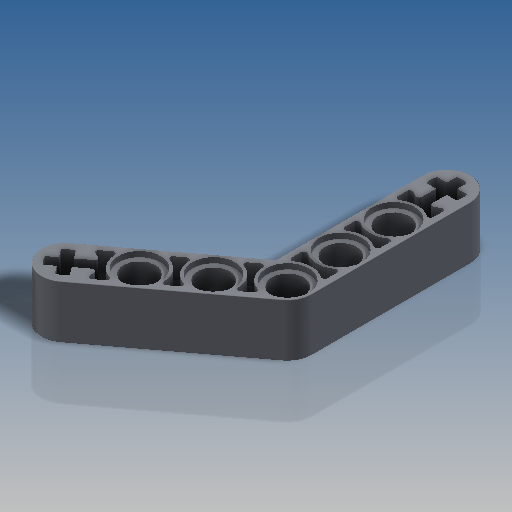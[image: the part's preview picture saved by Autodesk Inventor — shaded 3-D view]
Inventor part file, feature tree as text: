
AUTODESK INVENTOR PART (.ipt)
format: ipt  version: 2019.4 (Build 234330000, 330)  size: 444,928 bytes
history: native  units: mm
features: extrude x3, sketch x2, mirror x1, pattern_circular x1, fillet x1, projected_geometry x1
ambient origin geometry x8: Origin, YZ Plane, XZ Plane, XY Plane, X Axis, Y Axis, Z Axis, Center Point
bodies: Solid1 (feature_tree)
feature tree (9):
  extrude  "Extrusion1"  Depth=7.2mm
  sketch  "Sketch6"  dims[d41=0.8mm d42=0.0mm d43=3.1mm d44=0.0mm d49=6.4mm d50=4.8mm d51=8.0mm d52=0.9mm d60=0.4mm d61=0.1mm d62=1.6mm d63=30.0mm d65=8.0mm d66=10.0mm d68=10.0mm d72=20.0mm d73=22.142992mm]
  extrude  "Extrusion7"  Depth=3.1mm TaperAngle=0.0deg
  extrude  "Extrusion8"  Depth=6.4mm
  mirror  "Mirror1"
  pattern_circular  "Circular Pattern1"  [2 undecoded]
  fillet  "Fillet2"  Radius=8.0mm
  sketch  "Sketch1"  dims[d14=8.0mm d15=0.0mm d32=7.2mm]
  projected_geometry  "Projected Loop5"
note: 2 required parameter values undecoded (feature->parameter linkage not recoverable at this tier; creation-order binding heuristic only, values carry confidence <= 0.55)
